# Revit family: Gira_207500
name_source: partatom
category: Elektroinstallationen
revit_build: Autodesk Revit 2017 (Build: 20160225_1515(x64)
units: mm (PartAtom-declared; Revit-internal decimal feet)

## family parameters
Basisbauteil = Fläche
Beim Laden mit Abzugskörper schneiden = Nein
Bemaßung runder Anschluss = Durchmesser verwenden
Beschriftungsausrichtung beibehalten = Nein
Gemeinsam genutzt = Nein
Raumberechnungspunkt = Nein
Teiletyp = Normal

## types (1)
- Gira_207500
    Art des Zubehörs = sonstige
    BIM = https://media.stage.bim.site
    Beschreibung = Gira FacilityServer   Gateway für die KNX Installation, speziell auf die hohen Anforderungen im gewerblichen Bereich abgestimmt. Mit dem Gira FacilityServer lassen sich Anlagen und Gebäudegewerke intelligent miteinander vernetzen und die gesamte KNX Installation zentral vom PC aus kontrollieren, steuern und programmieren. Durch Anbindung an das Internet sind Zugriff und Überwachung von Gebäude- und Anlagentechnik auch von außerhalb möglich. Dient auch als Datenserver für übergeordnete Facility-Managementsysteme, denen er gespeicherte Verbrauchs- und Betriebsdaten zur Auswertung bereitstellt. Er bietet das komplette Leistungsspektrum des Gira HomeServers, ist aber für den Einsatz im gewerblichen Bereich mit deutlich mehr Speicherplatz ausgestattet. So lassen sich wesentlich größere Datenmengen speichern und komplexere, aufwändigere Visualisierungen erstellen. Mehrere Gira FacilityServer können vernetzt werden, um auch räumlich voneinander getrennte Gebäude miteinander zu verbinden: Lokale und übergeordnete Anwendungen lassen sich kombinieren. Neben dem PC kann ein Zugriff auch über andere internetfähige Geräte erfolgen, die an ein LAN, WLAN oder das Internet angeschlossen sind. Damit sind die KNX Funktionen überall kontrollier- und steuerbar. Als komfortable Bediengeräte eignen sich auch Gira Control 9 Client, Gira Control 19 Client 2 und Gira HomeServer App. Die App ist im Apple App Store und Google Play Store verfügbar und lässt sich auf Smartphones sowie auf Tablets verwenden.  Merkmale: - Updatefähig. - Einbau in 19-Rack. Hierfür ist im Lieferumfang ein 19-Einschub mit Aluminiumblende enthalten. Auch als Stand-alone-Gerät nutzbar. - Verwaltung von 200 Benutzern. Mehrfacher Login unter einem Benutzernamen möglich. - Archivierung von Projekten mit eigenen Inhalten, wie z. B. Grundrisszeichnungen etc. - Zyklische getriggerte Datenaufzeichnung (z. B. Temperaturverläufe, Betriebsstundenzähler, Füllstände). - Grafische Benutzeroberfläche: Visualisierung von Gebäude- bzw. Gerätezuständen mit frei positionierbaren Icons und Texten. Hinterlegen eigener Bilder und Menüstrukturen pro Benutzergruppe. - Auswertung von IP-Kameras: Aufzeichnung von Bildern und Darstellung in Visualisierung. Weiterleitung der Bild-Daten per E-Mail und FTP. Dabei sind länderspezifische Anforderungen zu berücksichtigen, insbesondere protokollspezifische Informationen und Normen im Kommunikationsbereich. - Export von Daten- bzw. Alarmaufzeichnungen im Format Excel(tm), CSV, HTML, XML. - Mathematische Funktionen (z. B. Grundrechenarten). - Speichern Abrufen von Lichtszenen. - Zeitschaltuhren, Wochenprogramm, Feiertagskalender. - Störmeldungen, Messwerte und Sensor- bzw. Aktorzustände per Push Notification und E-Mail übertragbar. Quittierung über KNX. - Selbstlernende Anwesenheitssimulation. - Fernprogrammierung per Netzwerk-, Internet-, DFÜ-Verbindung. - Senden von ASCII-Texten. - IP-Kopplung mit Fremdprodukten, die IP-Telegramme zur Steuerung erzeugen oder bearbeiten. - Verschleißarm. - Grafischer Logikeditor: Ermöglicht z. B. projektübergreifendes Kopieren von Bausteingruppen, Anlegen beliebig vieler Arbeitsblätter. Vorbereitet sind über 150 Logikbausteine. - Importieren und exportieren von globalen Bibliotheken. - Kommunikationsobjekte: Datenübernahme aus ETS per OPC-Datei oder direkt aus der knxproj-Datei. Im- und Export von Kommunikationsobjekten als CSV-Datei. - Universal-Zeitschaltuhr: Mehrere Schaltpunkte pro Uhr möglich. Verwendung von Platzhaltern in Tag, Monat, Jahr. Aktivierung Deaktivierung über Kommunikationsobjekt. Mit Astro- und Zufallsfunktion. - Datensicherung Wiederherstellung von Remanentdaten. - 14-Byte-KNX-Texte: Auswertung durch Vergleich mit Textstring. Verwendung in Push Notification, E-Mails, Statusseite. - Empfang von IP-Telegrammen: Angabe eines Adressbereichs, Extrahieren von 14-Byte-KNX-Texten, Zuordnung zu 14-Byte-KNX-Texten. - SNMP: Auslesen von numerischen und 14-Byte-KNX-Texten. Setzen von numerischen Werten, Integerwerten und Texten. Senden von SNMP-Traps über FacilityServer-Befehl. Optional ColdStart-Trap beim Start des FacilityServers. - Bedienung Statusanzeige über Agfeo-Telefonanlage. - Auswerten von webbasierten IP-Geräten (lesend schreibend). - Buszugriff mittels KNXnet IP Protokoll. - iETS-Server: Fernprogrammierung von KNX Anlagen. Freigabe der iETS-Funktion über Kommunikationsobjekt. Gira HomeServer läuft während der Programmierung über iETS ohne Einschränkung weiter. Schaltvorgänge werden weiter ausgeführt. Prozessabbild bleibt aktuell.  Hinweise : - Weitere Informationen: www.gira.de facilityserver. - Technische Angaben können je nach Versionsstand variieren bzw. verändert werden. Ebenso kann der Leistungsumfang zwischen den einzelnen Clients (QuadClient, iOS App, Android App) variieren. - Empfohlene Systemvoraussetzungen für Bediengeräte: Internet-Browser möglicher Bediengeräte müssen mindestens HTML 4.0, Java Script 1.1, CSS und Dynamic HTML unterstützen. - Gira FacilityServer Experten-Software für Betriebssysteme ab Windows XP(tm) inkl. Internet Explorer ab Version 6.0. - Übernahme der ETS-Gruppenadressen aus ETS 2, 3, 4 und 5. - Einbindung von Grafikprogrammen. - Der Gira AppShop ist der Marktplatz für interessante Lösungen und Anwendungen der intelligenten Gebäudetechnik. Inzwischen sind dort mehr als 200 Apps erhältlich, darunter Anwendungsbeschreibungen, Plug-ins, Funktionsvorlagen, Logikbausteine und Musterprojekte. Entdecken Sie jetzt Anwendungen für den Gira FacilityServer.   www.appshop.gira.de.
    Datenblatt = https://katalog.gira.de
    GTIN = 4010337051817
    HAN = 207500
    Hersteller = Gira
    Produktseite = http://katalog.gira.de
    Typname = Gira FacilityServer Gira Server
    URL = https://www.gira.de
    Vorgabe-Ansicht = 1219 mm

## geometry (parser evidence)
native form markers: Sweep x3
no freeform markers — native parametric forms only
